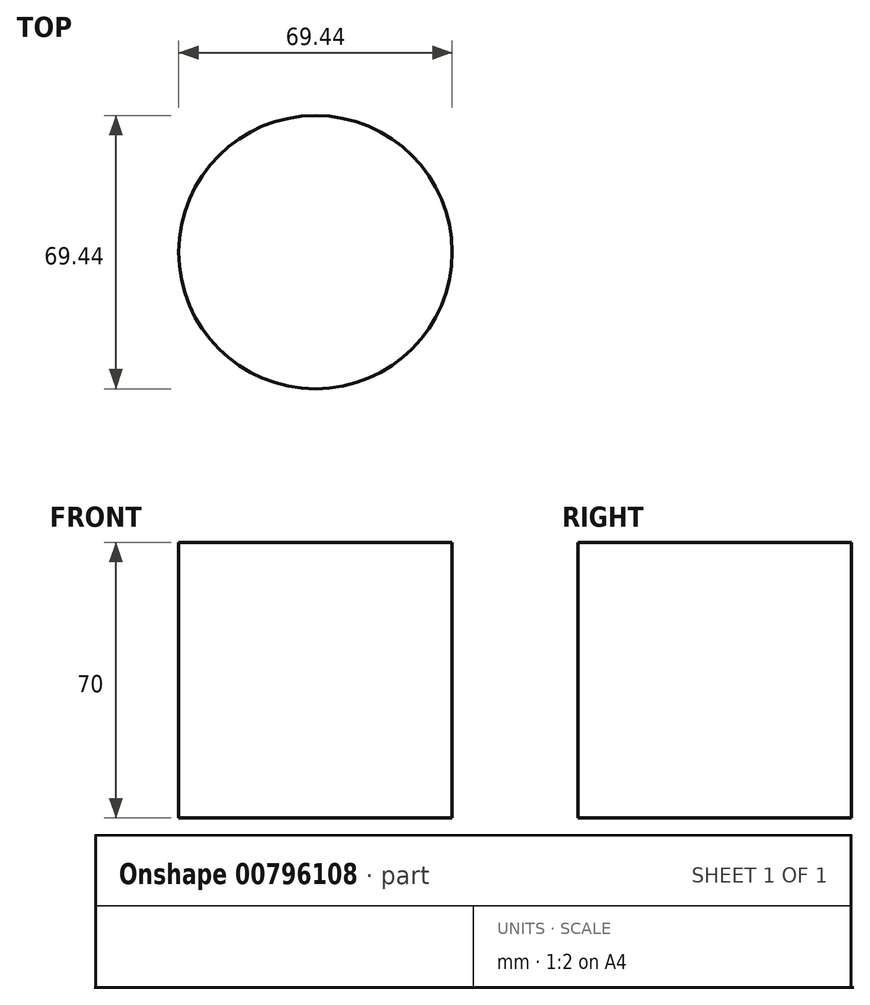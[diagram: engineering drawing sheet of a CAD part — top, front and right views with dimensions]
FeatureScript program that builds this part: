
annotation { "Feature Type Name" : "Feature", "Feature Type Description" : "" }
export const myFeature = defineFeature(function(context is Context, id is Id, definition is map)
    precondition{}
    {
        {
            var Q0;
            Q0=qCreatedBy(makeId("Top.planeOp"),FACE);
            var sketch = newSketch(context, id + "F0", { "sketchPlane" : qUnion([Q0])});
            skCircle(sketch, "E0", {"center": v(0, 0) * mm, "radius": 34.72 * mm});
            skSolve(sketch);
        }
        {
            var Q0;
            Q0=makeQuery(id+"F0.imprint","IMPRINT",FACE,{"disambiguationData":[TD([[makeQuery(id+"F0.imprint","IMPRINT",EDGE,{"derivedFrom":sQuery(id+"F0.wireOp",EDGE,"E0")}),1.0]])]});
            extrude(context, id + "F1", {"entities" : qUnion([Q0]), "depth" : 70 * mm, "offsetDistance" : 25 * mm});
        }
    });
